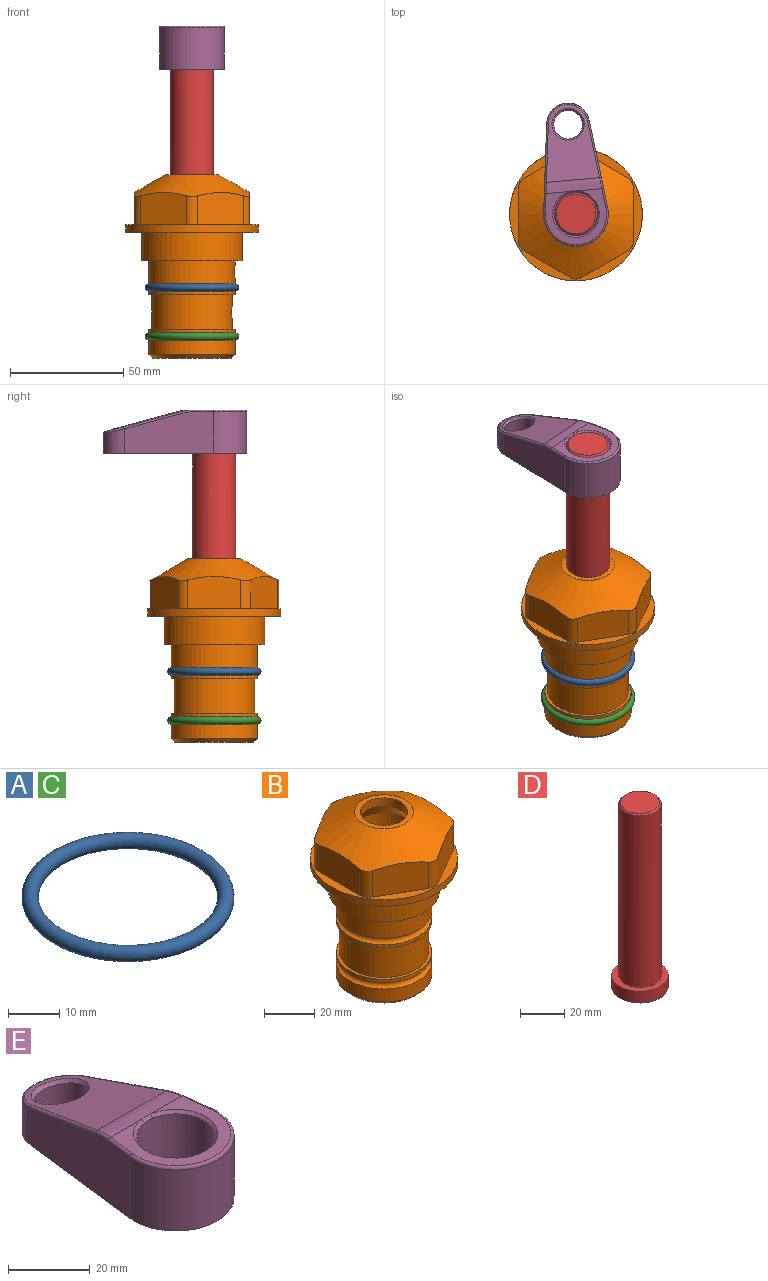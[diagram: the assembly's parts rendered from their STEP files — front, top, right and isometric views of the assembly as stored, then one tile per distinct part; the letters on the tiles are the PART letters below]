
ASSEMBLY  parts=5 mates=4
PART A: 1 faces, bbox 44.7x44.7x3.2 mm
  f0: torus R=19.05mm, axis (0,0,1), area 1193.9mm2
PART B: 36 faces, bbox 58.7x58.7x81 mm
  f0: cylinder r=17.78mm len=35.56mm, axis (0,0,1), area 1670.8mm2, adj f23,f24,f31
  f1: cylinder r=19.05mm len=38.1mm, axis (0,0,1), area 1191.9mm2, adj f26,f27,f30
  f2: plane 58.66x58.66mm, normal (0,0,-1), area 1150.6mm2, adj f3,f28
  f3: cylinder r=29.33mm len=58.66mm, axis (0,0,-1), area 585.1mm2, adj f2,f4
  f4: plane 58.66x58.66mm, normal (0,0,1), area 475.9mm2, adj f3,f5,f6,f7,f8,f9,f10,f11
  f5: plane 20.32x14.34mm, normal (-0.5,0.87,0), area 324.4mm2, adj f4,f15,f16,f17
  f6: plane 20.32x14.34mm, normal (0.5,0.87,0), area 324.4mm2, adj f4,f14,f15,f17
  f7: plane 23.48x14.34mm, normal (1,0,0), area 324.4mm2, adj f4,f13,f14,f17
  f8: plane 20.32x14.34mm, normal (0.5,-0.87,0), area 324.4mm2, adj f4,f12,f13,f17
  f9: plane 20.32x14.34mm, normal (-0.5,-0.87,0), area 324.4mm2, adj f4,f11,f12,f17
  f10: plane 23.48x14.34mm, normal (-1,0,0), area 324.4mm2, adj f4,f11,f16,f17
  f11: cylinder r=5.08mm len=12.85mm, axis (0,0,-1), area 67.2mm2, adj f4,f9,f10,f17
  f12: cylinder r=5.08mm len=12.85mm, axis (0,0,-1), area 67.2mm2, adj f4,f8,f9,f17
  f13: cylinder r=5.08mm len=12.85mm, axis (0,0,-1), area 67.2mm2, adj f4,f7,f8,f17
  f14: cylinder r=5.08mm len=12.85mm, axis (0,0,-1), area 67.2mm2, adj f4,f6,f7,f17
  f15: cylinder r=5.08mm len=12.85mm, axis (0,0,-1), area 67.2mm2, adj f4,f5,f6,f17
  f16: cylinder r=5.08mm len=12.85mm, axis (0,0,-1), area 67.2mm2, adj f4,f5,f10,f17
  f17: cone r=11.73mm half-angle=60deg, axis (0,0,-1), area 2071.8mm2, adj f5,f6,f7,f8,f9,f10,f11,f12
  f18: plane 23.46x23.46mm, normal (0,0,1), area 147.4mm2, adj f17,f35
  f19: plane 34.93x34.93mm, normal (0,0,-1), area 958mm2, adj f29
  f20: cylinder r=19.05mm len=38.1mm, axis (0,0,1), area 760.1mm2, adj f21,f29
  f21: torus R=19.05mm, axis (0,0,1), area 565.3mm2, adj f20,f22
  f22: cylinder r=19.05mm len=38.1mm, axis (0,0,1), area 190mm2, adj f21,f23
  f23: plane 38.1x38.1mm, normal (0,0,1), area 146.9mm2, adj f0,f22
  f24: plane 38.1x38.1mm, normal (0,0,-1), area 146.9mm2, adj f0,f25
  f25: cylinder r=19.05mm len=38.1mm, axis (0,0,1), area 190mm2, adj f24,f26
  f26: torus R=19.05mm, axis (0,0,1), area 565.3mm2, adj f1,f25
  f27: plane 44.45x44.45mm, normal (0,0,-1), area 411.7mm2, adj f1,f28
  f28: cylinder r=22.23mm len=44.45mm, axis (0,0,1), area 1773.5mm2, adj f2,f27
  f29: cone r=19.05mm half-angle=45deg, axis (0,0,1), area 257.5mm2, adj f19,f20
  f30: cylinder r=3.17mm len=6.75mm, axis (-1,0,0), area 128mm2, adj f1,f33
  f31: cylinder r=3.17mm len=6.35mm, axis (-1,0,0), area 102.5mm2, adj f0,f33
  f32: plane 25.4x25.4mm, normal (0,0,1), area 506.7mm2, adj f33
  f33: cylinder r=12.7mm len=66.42mm, axis (0,0,-1), area 5236.2mm2, adj f30,f31,f32,f34
  f34: cone r=9.53mm half-angle=30deg, axis (0,0,-1), area 443.4mm2, adj f33,f35
  f35: cylinder r=9.53mm len=19.05mm, axis (0,0,-1), area 240.9mm2, adj f18,f34
PART C: same geometry as A
PART D: 6 faces, bbox 25.4x25.4x101.6 mm
  f0: plane 17.46x17.46mm, normal (0,0,1), area 239.5mm2, adj f5
  f1: plane 25.4x25.4mm, normal (0,0,-1), area 506.7mm2, adj f2
  f2: cylinder r=12.7mm len=25.4mm, axis (0,0,1), area 506.7mm2, adj f1,f3
  f3: plane 25.4x25.4mm, normal (0,0,1), area 221.7mm2, adj f2,f4
  f4: cylinder r=9.53mm len=94.46mm, axis (0,0,1), area 5653mm2, adj f3,f5
  f5: cone r=8.73mm half-angle=45deg, axis (0,0,-1), area 64.4mm2, adj f0,f4
PART E: 31 faces, bbox 31.7x65.5x19.8 mm
  f0: plane 39.12x18.26mm, normal (0.99,0.12,0), area 612.2mm2, adj f1,f4,f7,f11,f13,f15
  f1: cylinder r=9.53mm len=18.91mm, axis (0,0,-1), area 296.1mm2, adj f0,f2,f7,f17
  f2: plane 39.12x18.26mm, normal (-0.99,0.12,0), area 612.2mm2, adj f1,f4,f7,f12,f14,f16
  f3: cylinder r=6.35mm len=12.7mm, axis (0,0,-1), area 362.4mm2, adj f7,f18
  f4: cylinder r=14.29mm len=28.58mm, axis (0,0,-1), area 882.2mm2, adj f0,f2,f7,f10
  f5: cylinder r=9.53mm len=19.05mm, axis (0,0,-1), area 1092.6mm2, adj f7,f19,f20
  f6: plane 26.99x23.69mm, normal (0,0,1), area 216.2mm2, adj f9,f10,f11,f12,f19
  f7: plane 63.5x28.58mm, normal (0,0,-1), area 661.8mm2, adj f0,f1,f2,f3,f4,f5,f22,f23
  f8: plane 33.52x23.6mm, normal (0,0.26,0.97), area 486mm2, adj f9,f15,f16,f17,f18
  f9: cylinder r=19.05mm len=24.72mm, axis (1,0,0), area 120.4mm2, adj f6,f8,f13,f14,f20
  f10: torus R=13.49mm, axis (0,0,1), area 59mm2, adj f4,f6,f11,f12
  f11: cylinder r=0.79mm len=8.67mm, axis (0.12,-0.99,0), area 10.8mm2, adj f0,f6,f10,f13
  f12: cylinder r=0.79mm len=8.67mm, axis (0.12,0.99,0), area 10.8mm2, adj f2,f6,f10,f14
  f13: bspline ~4.95x1.42mm, area 6.1mm2, adj f0,f9,f11,f15
  f14: bspline ~4.95x1.42mm, area 6.1mm2, adj f2,f9,f12,f16
  f15: cylinder r=0.79mm len=25.95mm, axis (0.12,-0.96,0.26), area 32.9mm2, adj f0,f8,f13,f17
  f16: cylinder r=0.79mm len=25.95mm, axis (0.12,0.96,-0.26), area 32.9mm2, adj f2,f8,f14,f17
  f17: bspline ~18.91x8.38mm, area 30mm2, adj f1,f8,f15,f16
  f18: bspline ~14.29x14.29mm, area 48.3mm2, adj f3,f8
  f19: cone r=9.53mm half-angle=45deg, axis (0,0,1), area 66.5mm2, adj f5,f6,f20
  f20: bspline ~3.22x0.96mm, area 3.5mm2, adj f5,f9,f19
  f21: plane 2.75x2.72mm, normal (0,0,-1), area 2.9mm2, adj f23,f25,f28
  f22: plane 23.05x15.88mm, normal (-0.99,-0.12,0), area 323.6mm2, adj f7,f25,f26,f27,f28,f29
  f23: plane 23.05x15.88mm, normal (0.99,-0.12,0), area 323.6mm2, adj f7,f21,f25,f27,f28,f30
  f24: cylinder r=9.53mm len=10.69mm, axis (0,0,-1), area 114.7mm2, adj f7,f27,f29,f30
  f25: cylinder r=12.7mm len=20.59mm, axis (0,0,-1), area 381.1mm2, adj f7,f21,f22,f23,f26,f28
  f26: plane 2.75x2.72mm, normal (0,0,-1), area 2.9mm2, adj f22,f25,f28
  f27: plane 19.72x18.37mm, normal (0,-0.26,-0.97), area 291.8mm2, adj f22,f23,f24,f28,f29,f30
  f28: cylinder r=15.88mm len=19.92mm, axis (1,0,0), area 54.8mm2, adj f21,f22,f23,f25,f26,f27
  f29: cylinder r=1.59mm len=11mm, axis (0,0,-1), area 34.7mm2, adj f7,f22,f24,f27
  f30: cylinder r=1.59mm len=11mm, axis (0,0,-1), area 34.7mm2, adj f7,f23,f24,f27
PLACE A at identity
PLACE B at identity fixed
PLACE C t=(0,0,-21.59)mm
PLACE D rot(axis=(0,0,1),5deg) t=(0,0,27.55)mm
PLACE E rot(axis=(0,0,1),5deg) t=(0,0,27.55)mm
MATE fastened C.f0 <-> B.f0  axis (0,0,1) through (0,0,-46.1)mm
MATE fastened A.f0 <-> B.f0  axis (0,0,1) through (0,0,-24.51)mm
MATE fastened E.f4 <-> D.f2  axis (0,0,1) through (0,0,91.05)mm
MATE cylindrical B.f0 <-> D.f2  axis (0,0,1) through (0,0,-50.55)mm
